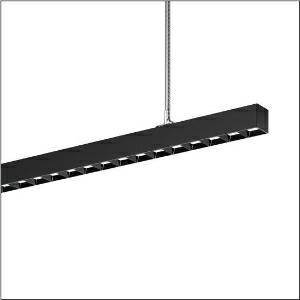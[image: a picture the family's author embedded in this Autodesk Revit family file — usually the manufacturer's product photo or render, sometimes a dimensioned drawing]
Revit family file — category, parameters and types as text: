
# Revit family: silica_r__21_51mx32tctdb_2a66
name_source: partatom
category: Lighting Fixtures
units: mm (PartAtom-declared; Revit-internal decimal feet)

## family parameters
Cut with Voids When Loaded = No
Host = Face
Light Source = No
Part Type = Normal
Room Calculation Point = No
Round Connector Dimension = Use Diameter
Shared = No

## types (1)
- --- (1 x LED, 15540 lm, 133.6 W, 6500K)
    Apparent Load = 134 VA
    CIE Flux Codes = 84 99 100 60 100
    Color Rendering = 80
    Color Temperature = 6500K
    Default Elevation = 1800 mm
    Description = Silica® 21, office luminaire, primary light control with darklight reflector, of PMMA, black, CAT 2 (L<= 3000cd/m²), light emission: direct/indirect distribution, primary light characteristic: symmetric, installation type: suspended mounting, LED, rated luminous flux: 15.540lm, luminous efficacy: 111lm/W, light colour: 8tw, colour temperature: 2700..6500K, control gear: DALI DT8, with terminal, 3+2-pole, max. 2.5mm², mains connection: 220..240V, AC, 50/60Hz, rated input power: 140.3W, luminaire housing, of aluminium, matt jet black (RAL 9005), length: 3.004mm, width: 53mm, height: 53mm, protection rating (complete): IP20, insulation class (complete): insulation class I (protective earthing), certification: CE, permissible operating ambient temperature: 0..+35°C, standard: EN 50419, packaging unit: 1 piece
    Height = 53 mm
    Lamp = 1 x LED
    Lamp Light Flux = 15540 lm
    Lamp Power = 133.6 W
    Lamp count = 1
    Length = 3004 mm
    Luminous efficacy = 116 lm/W
    Manufacturer = Siteco
    ModVariant = No
    Model = 51MX32TCTDB
    Mounting Place = Ceiling
    Mounting Type = Pendant
    Number of Poles = 1
    OnlyDefault = Yes
    Power Factor = 1
    Product Name = Silica® 21
    Product group = office luminaire | ceiling pendant
    ProductGroupID = 903
    Protection Class = Protection class I
    Protection Degree = IP 20
    RLX_Detail_Level = 1
    RLX_Emergency_Light_Flux = 0 lm
    RLX_Emergency_Type = 0
    RLX_Emergency_Type_DB = No
    RlxData = <blob elided: 62785 chars, md5=4f46b9fc>
    Socket = socket
    Standby Power = 0 W
    System Light Flux = 15540 lm
    System Power = 134 W
    Type Comments = individual setting
    Type Image = l_1335852.jpg
    URL = http://relux.com
    VarID = @adj_161411
    Voltage = 0 V
    Weight = 0.00 kg
    Width = 53 mm

## geometry (parser evidence)
native form markers: Blend x4, Sweep x13
no freeform markers — native parametric forms only
